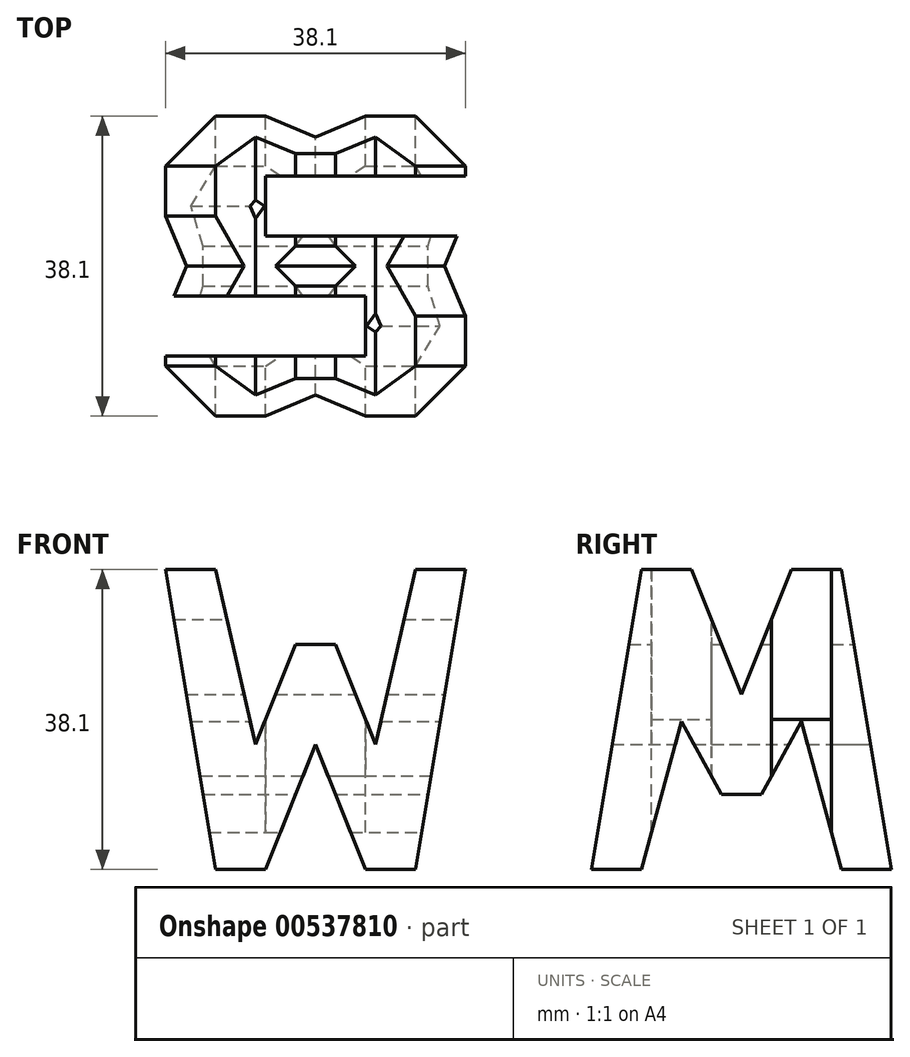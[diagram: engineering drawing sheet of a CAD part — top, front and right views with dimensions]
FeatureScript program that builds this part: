
annotation { "Feature Type Name" : "Feature", "Feature Type Description" : "" }
export const myFeature = defineFeature(function(context is Context, id is Id, definition is map)
    precondition{}
    {
        {
            var Q0;
            Q0=qCreatedBy(makeId("Front.planeOp"),FACE);
            var sketch = newSketch(context, id + "F0", { "sketchPlane" : qUnion([Q0])});
            skLineSegment(sketch, "E0", {"start": v(0, 0) * mm, "end": v(0, 38.1) * mm});
            skLineSegment(sketch, "E1", {"start": v(0, 0) * mm, "end": v(38.1, 0) * mm});
            skLineSegment(sketch, "E2", {"start": v(38.1, 0) * mm, "end": v(38.1, 38.1) * mm});
            skLineSegment(sketch, "E3", {"start": v(38.1, 38.1) * mm, "end": v(0, 38.1) * mm});
            skSolve(sketch);
        }
        {
            var Q0;
            Q0 = qSketchRegion(id + "F0", true);
            extrude(context, id + "F1", {"entities" : qUnion([Q0]), "depth" : 38.1 * mm, "offsetDistance" : 25.4 * mm});
        }
        {
            var Q0;
            Q0=qCreatedBy(makeId("Right.planeOp"),FACE);
            cPlane(context, id + "F2", {"entities" : qUnion([Q0]), "cplaneType" : CPlaneType.OFFSET, "offset" : 38.1 * mm, "width" : 152.4 * mm, "height" : 152.4 * mm});
        }
        {
            var Q0;
            Q0=qCreatedBy(makeId("Top.planeOp"),FACE);
            cPlane(context, id + "F3", {"entities" : qUnion([Q0]), "cplaneType" : CPlaneType.OFFSET, "offset" : 38.1 * mm, "width" : 152.4 * mm, "height" : 152.4 * mm});
        }
        {
            var Q0;
            Q0=makeQuery(id+"F1.opExtrude","CAP_FACE",FACE,{"disambiguationData":[OSD([sQuery(id+"F0.wireOp",EDGE,"E0"),sQuery(id+"F0.wireOp",EDGE,"E1"),sQuery(id+"F0.wireOp",EDGE,"E2"),sQuery(id+"F0.wireOp",EDGE,"E3")])],"isStart":true});
            var sketch = newSketch(context, id + "F4", { "sketchPlane" : qUnion([Q0])});
            skLineSegment(sketch, "E4", {"start": v(-38.1, 38.1) * mm, "end": v(-31.75, 0) * mm});
            skLineSegment(sketch, "E5", {"start": v(-31.75, 38.1) * mm, "end": v(-26.67, 15.87) * mm});
            skLineSegment(sketch, "E6", {"start": v(-26.67, 15.87) * mm, "end": v(-21.59, 28.58) * mm});
            skLineSegment(sketch, "E7", {"start": v(-21.59, 28.58) * mm, "end": v(-16.5, 28.58) * mm});
            skLineSegment(sketch, "E8", {"start": v(-16.5, 28.58) * mm, "end": v(-11.43, 15.88) * mm});
            skLineSegment(sketch, "E9", {"start": v(-11.43, 15.88) * mm, "end": v(-6.35, 38.1) * mm});
            skLineSegment(sketch, "E10", {"start": v(0, 38.1) * mm, "end": v(-6.35, 0) * mm});
            skLineSegment(sketch, "E11", {"start": v(-31.75, 0) * mm, "end": v(-25.4, 0) * mm});
            skLineSegment(sketch, "E12", {"start": v(-25.4, 0) * mm, "end": v(-19.05, 15.88) * mm});
            skLineSegment(sketch, "E13", {"start": v(-19.05, 15.88) * mm, "end": v(-12.7, 0) * mm});
            skLineSegment(sketch, "E14", {"start": v(-12.7, 0) * mm, "end": v(-6.35, 0) * mm});
            skLineSegment(sketch, "E15", {"start": v(-38.1, 38.1) * mm, "end": v(-31.75, 38.1) * mm});
            skLineSegment(sketch, "E16", {"start": v(-6.35, 38.1) * mm, "end": v(0, 38.1) * mm});
            skSolve(sketch);
        }
        {
            var Q0;
            {var subQ0=sQuery(id+"F4.wireOp",EDGE,"E5");Q0=makeQuery(id+"F4.imprint","IMPRINT",FACE,{"disambiguationData":[TD([[makeQuery(id+"F4.imprint","IMPRINT",EDGE,{"derivedFrom":subQ0}),1.0]])]});}
            var Q1;
            {var subQ0=sQuery(id+"F4.wireOp",EDGE,"E4");Q1=makeQuery(id+"F4.imprint","IMPRINT",FACE,{"disambiguationData":[TD([[makeQuery(id+"F4.imprint","IMPRINT",EDGE,{"derivedFrom":subQ0}),-1.0]])]});}
            var Q2;
            {var subQ0=sQuery(id+"F4.wireOp",EDGE,"E12");Q2=makeQuery(id+"F4.imprint","IMPRINT",FACE,{"disambiguationData":[TD([[makeQuery(id+"F4.imprint","IMPRINT",EDGE,{"derivedFrom":subQ0}),-1.0]])]});}
            var Q3;
            {var subQ0=sQuery(id+"F4.wireOp",EDGE,"E10");Q3=makeQuery(id+"F4.imprint","IMPRINT",FACE,{"disambiguationData":[TD([[makeQuery(id+"F4.imprint","IMPRINT",EDGE,{"derivedFrom":subQ0}),1.0]])]});}
            extrude(context, id + "F5", {"entities" : qUnion([Q0, Q1, Q2, Q3]), "operationType" : NewBodyOperationType.REMOVE, "oppositeDirection" : true, "depth" : 38.1 * mm, "offsetDistance" : 25.4 * mm});
        }
        {
            var Q0;
            Q0=qCreatedBy(id+"F2.planeOp",FACE);
            var sketch = newSketch(context, id + "F6", { "sketchPlane" : qUnion([Q0])});
            skLineSegment(sketch, "E17", {"start": v(0, 0) * mm, "end": v(-6.35, 38.1) * mm});
            skLineSegment(sketch, "E18", {"start": v(-6.35, 38.1) * mm, "end": v(-12.7, 38.1) * mm});
            skLineSegment(sketch, "E19", {"start": v(-12.7, 38.1) * mm, "end": v(-19.05, 22.22) * mm});
            skLineSegment(sketch, "E20", {"start": v(-19.05, 22.22) * mm, "end": v(-25.4, 38.1) * mm});
            skLineSegment(sketch, "E21", {"start": v(-25.4, 38.1) * mm, "end": v(-31.75, 38.1) * mm});
            skLineSegment(sketch, "E22", {"start": v(-31.75, 38.1) * mm, "end": v(-38.1, 0) * mm});
            skLineSegment(sketch, "E23", {"start": v(-31.75, 0) * mm, "end": v(-26.67, 18.8) * mm});
            skLineSegment(sketch, "E24", {"start": v(-26.67, 18.8) * mm, "end": v(-21.59, 9.52) * mm});
            skLineSegment(sketch, "E25", {"start": v(-21.59, 9.53) * mm, "end": v(-16.5, 9.53) * mm});
            skLineSegment(sketch, "E26", {"start": v(-16.5, 9.52) * mm, "end": v(-11.43, 18.8) * mm});
            skLineSegment(sketch, "E27", {"start": v(-11.43, 18.8) * mm, "end": v(-6.35, 0) * mm});
            skLineSegment(sketch, "E28", {"start": v(-6.35, 0) * mm, "end": v(0, 0) * mm});
            skLineSegment(sketch, "E29", {"start": v(-38.1, 0) * mm, "end": v(-31.75, 0) * mm});
            skLineSegment(sketch, "E30.bottom", {"start": v(-38.1, 0) * mm, "end": v(0, 0) * mm});
            skLineSegment(sketch, "E30.top", {"start": v(-38.1, 38.1) * mm, "end": v(0, 38.1) * mm});
            skLineSegment(sketch, "E30.left", {"start": v(-38.1, 0) * mm, "end": v(-38.1, 38.1) * mm});
            skLineSegment(sketch, "E30.right", {"start": v(0, 0) * mm, "end": v(0, 38.1) * mm});
            skSolve(sketch);
        }
        {
            var Q0;
            {var subQ0=sQuery(id+"F6.wireOp",EDGE,"E22");Q0=makeQuery(id+"F6.imprint","IMPRINT",FACE,{"disambiguationData":[TD([[makeQuery(id+"F6.imprint","IMPRINT",EDGE,{"derivedFrom":subQ0}),-1.0]])]});}
            var Q1;
            {var subQ0=sQuery(id+"F6.wireOp",EDGE,"E19");Q1=makeQuery(id+"F6.imprint","IMPRINT",FACE,{"disambiguationData":[TD([[makeQuery(id+"F6.imprint","IMPRINT",EDGE,{"derivedFrom":subQ0}),-1.0]])]});}
            var Q2;
            {var subQ0=sQuery(id+"F6.wireOp",EDGE,"E17");Q2=makeQuery(id+"F6.imprint","IMPRINT",FACE,{"disambiguationData":[TD([[makeQuery(id+"F6.imprint","IMPRINT",EDGE,{"derivedFrom":subQ0}),-1.0]])]});}
            var Q3;
            {var subQ0=sQuery(id+"F6.wireOp",EDGE,"E23");Q3=makeQuery(id+"F6.imprint","IMPRINT",FACE,{"disambiguationData":[TD([[makeQuery(id+"F6.imprint","IMPRINT",EDGE,{"derivedFrom":subQ0}),-1.0]])]});}
            extrude(context, id + "F7", {"entities" : qUnion([Q0, Q1, Q2, Q3]), "operationType" : NewBodyOperationType.REMOVE, "oppositeDirection" : true, "depth" : 38.1 * mm, "offsetDistance" : 25.4 * mm});
        }
        {
            var Q0;
            Q0=qCreatedBy(id+"F3.planeOp",FACE);
            var sketch = newSketch(context, id + "F8", { "sketchPlane" : qUnion([Q0])});
            skLineSegment(sketch, "E31", {"start": v(48.39, -7.62) * mm, "end": v(12.7, -7.62) * mm});
            skLineSegment(sketch, "E32", {"start": v(12.7, -7.62) * mm, "end": v(12.7, -15.24) * mm});
            skLineSegment(sketch, "E33", {"start": v(12.7, -15.24) * mm, "end": v(48.47, -15.24) * mm});
            skLineSegment(sketch, "E34", {"start": v(0, -22.86) * mm, "end": v(25.4, -22.86) * mm});
            skLineSegment(sketch, "E35", {"start": v(25.4, -22.86) * mm, "end": v(25.4, -30.48) * mm});
            skLineSegment(sketch, "E36", {"start": v(25.4, -30.48) * mm, "end": v(0, -30.48) * mm});
            skLineSegment(sketch, "E37", {"start": v(0, 0) * mm, "end": v(38.1, 0) * mm});
            skLineSegment(sketch, "E38", {"start": v(38.1, 0) * mm, "end": v(38.1, -38.1) * mm});
            skLineSegment(sketch, "E39", {"start": v(38.1, -38.1) * mm, "end": v(0, -38.1) * mm});
            skLineSegment(sketch, "E40", {"start": v(0, -38.1) * mm, "end": v(0, 0) * mm});
            skSolve(sketch);
        }
        {
            var Q0;
            {var subQ0=sQuery(id+"F8.wireOp",EDGE,"E32");Q0=makeQuery(id+"F8.imprint","IMPRINT",FACE,{"disambiguationData":[TD([[makeQuery(id+"F8.imprint","IMPRINT",EDGE,{"derivedFrom":subQ0}),1.0]])]});}
            var Q1;
            {var subQ0=sQuery(id+"F8.wireOp",EDGE,"E34");Q1=makeQuery(id+"F8.imprint","IMPRINT",FACE,{"disambiguationData":[TD([[makeQuery(id+"F8.imprint","IMPRINT",EDGE,{"derivedFrom":subQ0}),-1.0]])]});}
            extrude(context, id + "F9", {"entities" : qUnion([Q0, Q1]), "operationType" : NewBodyOperationType.REMOVE, "oppositeDirection" : true, "depth" : 38.1 * mm, "offsetDistance" : 25.4 * mm});
        }
    });
